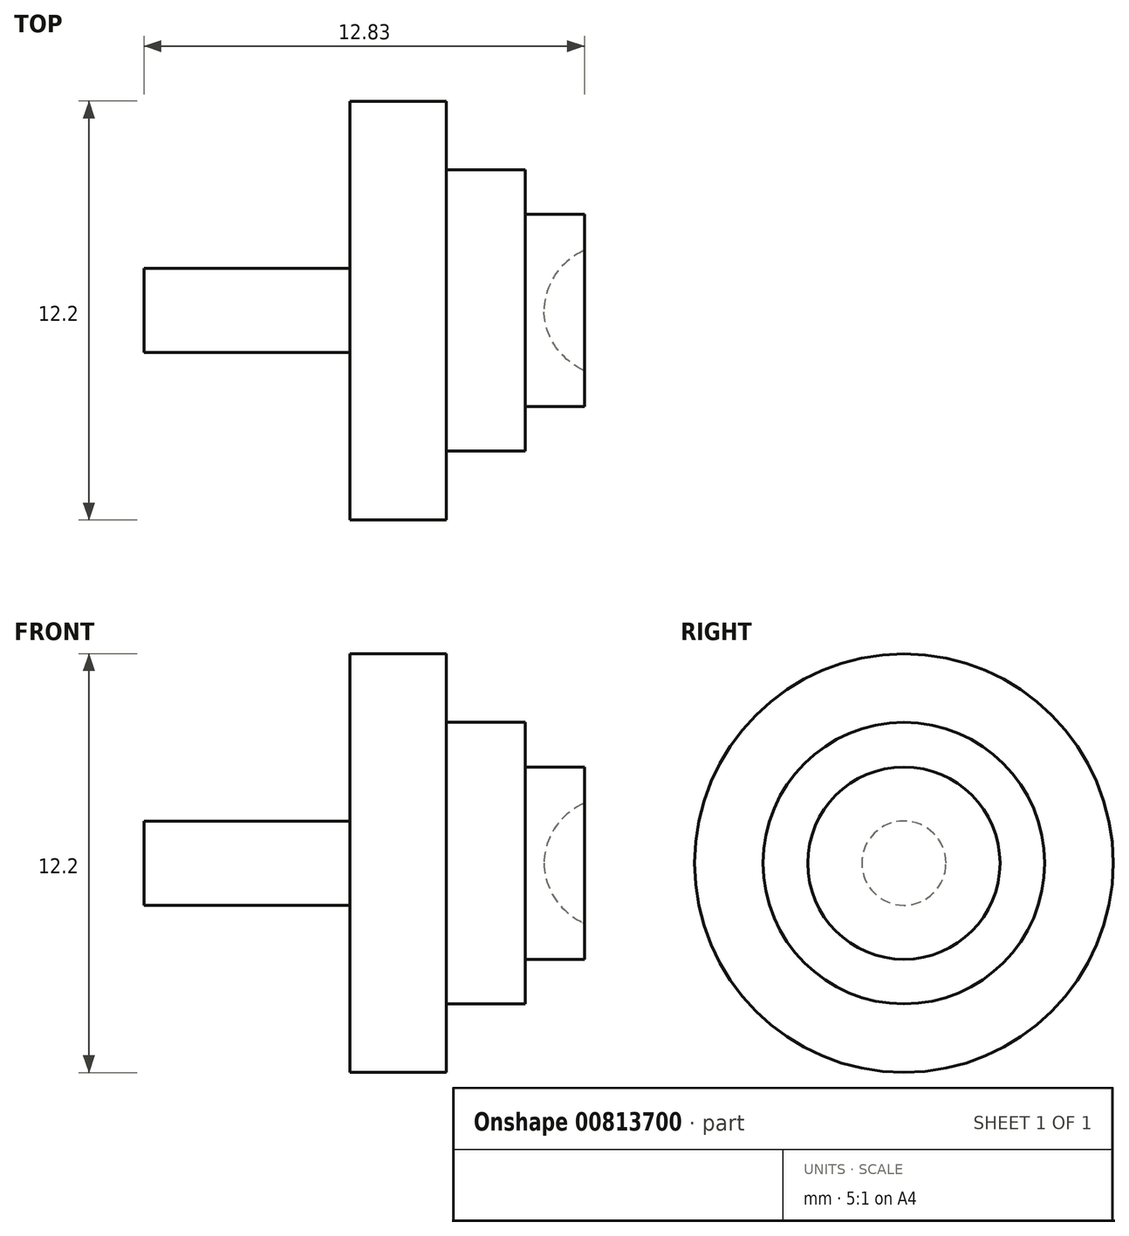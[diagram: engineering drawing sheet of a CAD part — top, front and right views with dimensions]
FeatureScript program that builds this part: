
annotation { "Feature Type Name" : "Feature", "Feature Type Description" : "" }
export const myFeature = defineFeature(function(context is Context, id is Id, definition is map)
    precondition{}
    {
        {
            var Q0;
            Q0=qCreatedBy(makeId("Front.planeOp"),FACE);
            var sketch = newSketch(context, id + "F0", { "sketchPlane" : qUnion([Q0])});
            skLineSegment(sketch, "E0", {"start": v(0.3, 4.1) * mm, "end": v(2.6, 4.1) * mm});
            skPoint(sketch, "E1.top.start.orphan", {"position": v(2.5, -6.1) * mm});
            skPoint(sketch, "E2.orphan", {"position": v(-2.63, -5.64) * mm});
            skPoint(sketch, "E3.trimOffspring.start.orphan", {"position": v(0, 0) * mm});
            skLineSegment(sketch, "E4", {"start": v(0.3, 6.1) * mm, "end": v(0.3, 4.1) * mm});
            skPoint(sketch, "E1.bottom.end.orphan", {"position": v(-2.5, 6.1) * mm});
            skLineSegment(sketch, "E5", {"start": v(0.3, 6.1) * mm, "end": v(-2.5, 6.1) * mm});
            skLineSegment(sketch, "E6", {"start": v(-2.5, 6.1) * mm, "end": v(-2.5, 1.75) * mm});
            skLineSegment(sketch, "E7", {"start": v(0, 0) * mm, "end": v(-2.5, 0) * mm, "construction": true});
            skLineSegment(sketch, "E8", {"start": v(0, 0) * mm, "end": v(2.6, 0) * mm, "construction": true});
            skLineSegment(sketch, "E9", {"start": v(2.6, 4.1) * mm, "end": v(2.6, 2.8) * mm});
            skLineSegment(sketch, "E10", {"start": v(4.33, 2.8) * mm, "end": v(2.6, 2.8) * mm});
            skLineSegment(sketch, "E11", {"start": v(4.33, 1.75) * mm, "end": v(4.33, 2.8) * mm});
            skPoint(sketch, "E12.start.orphan", {"position": v(4.6, 0) * mm});
            skPoint(sketch, "E13.orphan", {"position": v(4.33, 1.75) * mm});
            skLineSegment(sketch, "E14", {"start": v(-2.5, 1.75) * mm, "end": v(-2.5, 1.22) * mm});
            skLineSegment(sketch, "E15", {"start": v(-2.5, 0) * mm, "end": v(3.15, 0) * mm});
            skLineSegment(sketch, "E16", {"start": v(-8.5, 0) * mm, "end": v(-8.5, 1.22) * mm});
            skLineSegment(sketch, "E17", {"start": v(-8.5, 1.22) * mm, "end": v(-2.5, 1.22) * mm});
            skLineSegment(sketch, "E18", {"start": v(-8.5, 0) * mm, "end": v(-2.5, 0) * mm});
            skLineSegment(sketch, "E19", {"start": v(3.15, 0) * mm, "end": v(2.33, 0) * mm, "construction": true});
            skLineSegment(sketch, "E20", {"start": v(4.33, 1.8) * mm, "end": v(4.33, 2) * mm, "construction": true});
            skArc(sketch, "E21", {"start": v(4.29, 1.73) * mm, "mid": v(3.47, 1.03) * mm, "end": v(3.15, 0) * mm});
            skPoint(sketch, "E22.orphan", {"position": v(4.33, 0) * mm});
            skArc(sketch, "E23.filletArc", {"start": v(4.29, 1.73) * mm, "mid": v(4.32, 1.76) * mm, "end": v(4.33, 1.8) * mm});
            skPoint(sketch, "E24.MirrorCS.end.orphan", {"position": v(2.6, -4.1) * mm});
            skPoint(sketch, "E24.MirrorCS.start.orphan", {"position": v(0.3, -4.1) * mm});
            skPoint(sketch, "E25.MirrorCS.start.orphan", {"position": v(-2.5, -6.1) * mm});
            skPoint(sketch, "E26.MirrorCS.start.orphan", {"position": v(0.3, -6.1) * mm});
            skSolve(sketch);
        }
        {
            var Q0;
            Q0 = qSketchRegion(id + "F0", true);
            var Q1;
            Q1=sQuery(id+"F0.wireOp",EDGE,"E15");
            revolve(context, id + "F1", {"surfaceOperationType" : NewSurfaceOperationType.NEW, "entities" : qUnion([Q0]), "axis" : qUnion([Q1]), "revolveType" : RevolveType.FULL});
        }
    });
